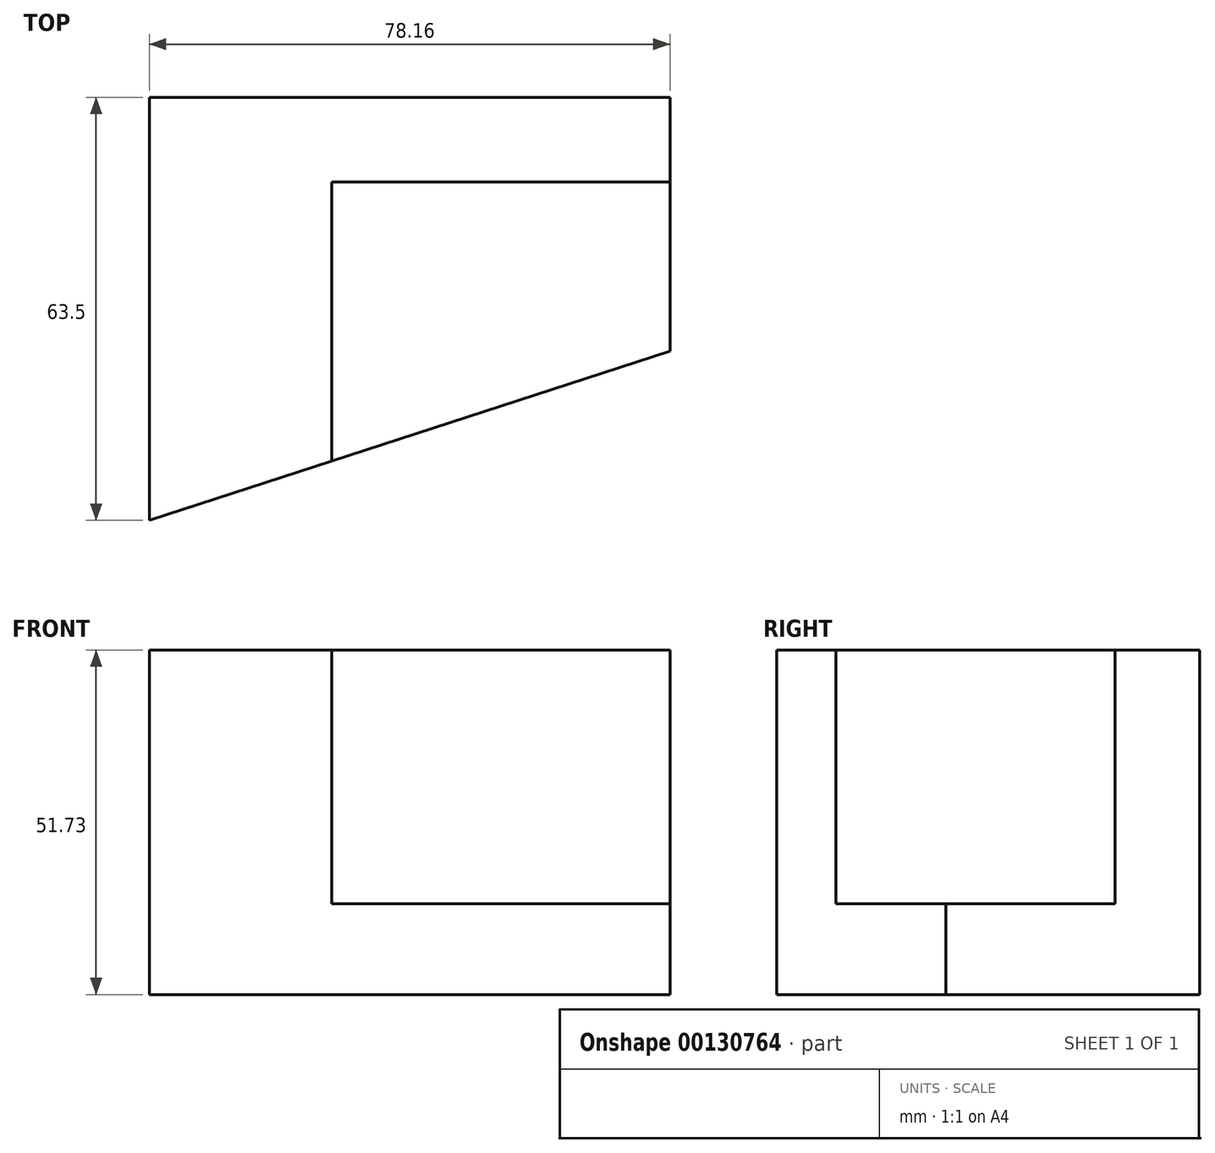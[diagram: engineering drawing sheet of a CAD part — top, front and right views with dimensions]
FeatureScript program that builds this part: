
annotation { "Feature Type Name" : "Feature", "Feature Type Description" : "" }
export const myFeature = defineFeature(function(context is Context, id is Id, definition is map)
    precondition{}
    {
        {
            var Q0;
            Q0=qCreatedBy(makeId("Front.planeOp"),FACE);
            var sketch = newSketch(context, id + "F0", { "sketchPlane" : qUnion([Q0])});
            skLineSegment(sketch, "E0", {"start": v(0, 0) * mm, "end": v(0, 51.73) * mm});
            skLineSegment(sketch, "E1", {"start": v(0, 51.73) * mm, "end": v(78.16, 51.73) * mm});
            skLineSegment(sketch, "E2", {"start": v(78.16, 51.73) * mm, "end": v(78.16, 0) * mm});
            skLineSegment(sketch, "E3", {"start": v(78.16, 0) * mm, "end": v(0, 0) * mm});
            skSolve(sketch);
        }
        {
            var Q0;
            Q0 = qSketchRegion(id + "F0", true);
            extrude(context, id + "F1", {"entities" : qUnion([Q0]), "oppositeDirection" : true, "depth" : 63.5 * mm});
        }
        {
            var Q0;
            Q0=makeQuery(id+"F1.opExtrude","SWEPT_FACE",FACE,{"disambiguationData":[OSD([sQuery(id+"F0.wireOp",EDGE,"E1")])]});
            var sketch = newSketch(context, id + "F2", { "sketchPlane" : qUnion([Q0])});
            skLineSegment(sketch, "E4", {"start": v(0, 0) * mm, "end": v(78.16, 25.4) * mm});
            skLineSegment(sketch, "E5", {"start": v(78.16, 25.4) * mm, "end": v(78.16, 0) * mm});
            skLineSegment(sketch, "E6", {"start": v(78.16, 0) * mm, "end": v(0, 0) * mm});
            skSolve(sketch);
        }
        {
            var Q0;
            Q0 = qSketchRegion(id + "F2", true);
            extrude(context, id + "F3", {"entities" : qUnion([Q0]), "operationType" : NewBodyOperationType.REMOVE, "endBound" : BoundingType.THROUGH_ALL, "oppositeDirection" : true, "depth" : 25.4 * mm});
        }
        {
            var Q0;
            Q0=qCreatedBy(makeId("Front.planeOp"),FACE);
            var sketch = newSketch(context, id + "F4", { "sketchPlane" : qUnion([Q0])});
            skLineSegment(sketch, "E7", {"start": v(27.36, 13.63) * mm, "end": v(27.36, 51.73) * mm});
            skLineSegment(sketch, "E8", {"start": v(27.36, 51.73) * mm, "end": v(78.16, 51.73) * mm});
            skLineSegment(sketch, "E9", {"start": v(78.16, 51.73) * mm, "end": v(78.16, 13.63) * mm});
            skLineSegment(sketch, "E10", {"start": v(78.16, 13.63) * mm, "end": v(27.36, 13.63) * mm});
            skSolve(sketch);
        }
        {
            var Q0;
            Q0 = qSketchRegion(id + "F4", true);
            extrude(context, id + "F5", {"entities" : qUnion([Q0]), "operationType" : NewBodyOperationType.REMOVE, "oppositeDirection" : true, "depth" : 50.8 * mm});
        }
    });
